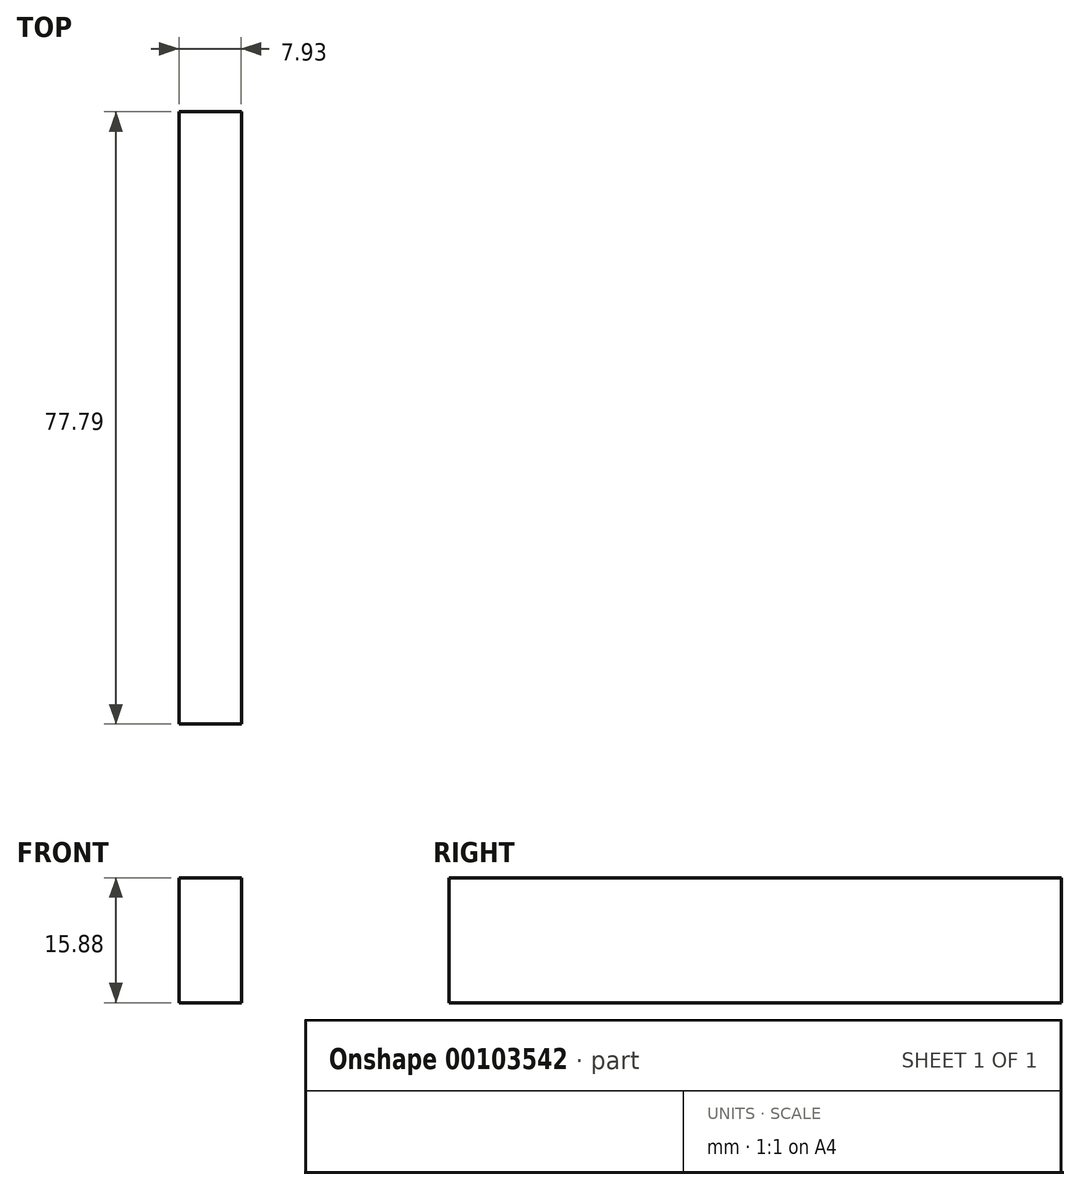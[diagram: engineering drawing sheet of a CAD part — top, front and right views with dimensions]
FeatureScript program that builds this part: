
annotation { "Feature Type Name" : "Feature", "Feature Type Description" : "" }
export const myFeature = defineFeature(function(context is Context, id is Id, definition is map)
    precondition{}
    {
        {
            var Q0;
            Q0=qCreatedBy(makeId("Front.planeOp"),FACE);
            var sketch = newSketch(context, id + "F0", { "sketchPlane" : qUnion([Q0])});
            skLineSegment(sketch, "E0.bottom", {"start": v(-34.85, 25.46) * mm, "end": v(-26.92, 25.46) * mm});
            skLineSegment(sketch, "E0.top", {"start": v(-34.85, 9.58) * mm, "end": v(-26.92, 9.58) * mm});
            skLineSegment(sketch, "E0.left", {"start": v(-34.85, 25.46) * mm, "end": v(-34.85, 9.58) * mm});
            skLineSegment(sketch, "E0.right", {"start": v(-26.92, 25.46) * mm, "end": v(-26.92, 9.58) * mm});
            skSolve(sketch);
        }
        {
            var Q0;
            Q0=makeQuery(id+"F0.imprint","IMPRINT",FACE,{"disambiguationData":[TD([[makeQuery(id+"F0.imprint","IMPRINT",EDGE,{"derivedFrom":sQuery(id+"F0.wireOp",EDGE,"E0.bottom")}),-1.0]])]});
            extrude(context, id + "F1", {"entities" : qUnion([Q0]), "depth" : 77.8 * mm});
        }
    });
